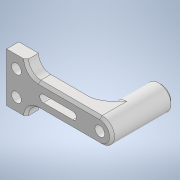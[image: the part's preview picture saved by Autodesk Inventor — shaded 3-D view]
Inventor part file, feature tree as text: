
AUTODESK INVENTOR PART (.ipt)
format: ipt  version: 2020 (Build 240168000, 168)  size: 196,096 bytes
history: native  units: mm
features: extrude x6, sketch x6, projected_geometry x4, other x4, fillet x2, reference x1
ambient origin geometry x8: Origin, YZ Plane, XZ Plane, XY Plane, X Axis, Y Axis, Z Axis, Center Point
bodies: Solid1 (feature_tree)
feature tree (23):
  extrude  "Extrusion1"  Depth=10.0mm TaperAngle=0.0deg
  extrude  "Extrusion2"  Depth=10.0mm
  extrude  "Extrusion3"  Depth=5.0mm TaperAngle=0.0deg
  fillet  "Fillet1"  Radius=6.0mm
  extrude  "Extrusion4"  Depth=8.0mm
  extrude  "Extrusion5"  Depth=5.0mm TaperAngle=0.0deg
  fillet  "Fillet2"  Radius=5.0mm
  extrude  "Extrusion6"  Depth=3.0mm
  sketch  "Sketch1"  dims[d0=10.0mm d1=20.0mm d2=0.0mm]
  reference  "Reference1"
  sketch  "Sketch2"  dims[d3=30.0mm d4=10.0mm]
  projected_geometry  "Projected Loop1"
  sketch  "Sketch3"  dims[d5=5.0mm d6=0.0mm d7=5.0mm d8=0.0mm d9=6.0mm]
  sketch  "Sketch4"  dims[d10=4.0mm d11=8.0mm]
  projected_geometry  "Projected Loop2"
  sketch  "Sketch5"  dims[d12=20.0mm d13=5.0mm d14=0.0mm d15=5.0mm]
  projected_geometry  "Projected Loop3"
  sketch  "Sketch6"  dims[d16=5.0mm d17=4.0mm d18=4.0mm d19=5.0mm d20=0.0mm d21=5.0mm d22=17.0mm d23=6.0mm d24=3.0mm d25=8.0mm d26=0.0mm]
  projected_geometry  "Projected Loop4"
  parser-record x1  (decoder bookkeeping rows leaked as tree rows — omitted from the tree; the rows remain in map.json)
  other  "delta_1.iam"
  other  "arm_shift_1:3"
  other  "motor_holder_1:1"
note: 1 file-system path scrubbed to <path> (originals preserved in map.json)
